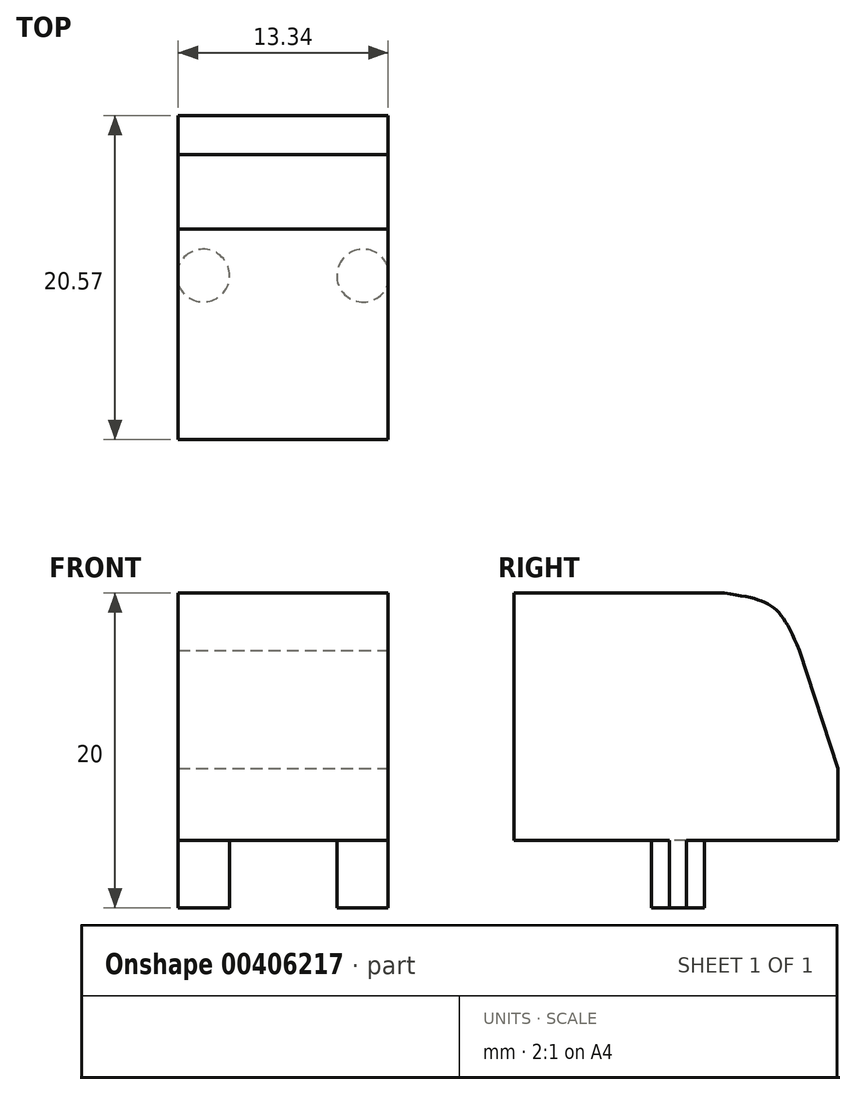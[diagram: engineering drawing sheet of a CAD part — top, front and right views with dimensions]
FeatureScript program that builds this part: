
annotation { "Feature Type Name" : "Feature", "Feature Type Description" : "" }
export const myFeature = defineFeature(function(context is Context, id is Id, definition is map)
    precondition{}
    {
        {
            var Q0;
            Q0=qCreatedBy(makeId("Front.planeOp"),FACE);
            var sketch = newSketch(context, id + "F0", { "sketchPlane" : qUnion([Q0])});
            skLineSegment(sketch, "E0.bottom", {"start": v(6.67, -7.85) * mm, "end": v(-6.67, -7.85) * mm});
            skLineSegment(sketch, "E0.top", {"start": v(6.67, 7.85) * mm, "end": v(-6.67, 7.85) * mm});
            skLineSegment(sketch, "E0.left", {"start": v(6.67, -7.85) * mm, "end": v(6.67, 7.85) * mm});
            skLineSegment(sketch, "E0.right", {"start": v(-6.67, -7.85) * mm, "end": v(-6.67, 7.85) * mm});
            skPoint(sketch, "E0.middle", {"position": v(0, 0) * mm});
            skSolve(sketch);
        }
        {
            var Q0;
            Q0=makeQuery(id+"F0.imprint","IMPRINT",FACE,{"disambiguationData":[TD([[makeQuery(id+"F0.imprint","IMPRINT",EDGE,{"derivedFrom":sQuery(id+"F0.wireOp",EDGE,"E0.bottom")}),-1.0]])]});
            extrude(context, id + "F1", {"entities" : qUnion([Q0]), "oppositeDirection" : true, "depth" : 20.57 * mm});
        }
        {
            var Q0;
            Q0=makeQuery(id+"F1.opExtrude","SWEPT_FACE",FACE,{"disambiguationData":[OSD([sQuery(id+"F0.wireOp",EDGE,"E0.bottom")])]});
            var sketch = newSketch(context, id + "F2", { "sketchPlane" : qUnion([Q0])});
            skLineSegment(sketch, "E1", {"start": v(0, 0) * mm, "end": v(0, -10.4) * mm, "construction": true});
            skPoint(sketch, "E1.endSnap0", {"position": v(0, 0) * mm});
            skLineSegment(sketch, "E2", {"start": v(0, -10.4) * mm, "end": v(5.08, -10.4) * mm, "construction": true});
            skLineSegment(sketch, "E3.MirrorCS", {"start": v(0, -10.4) * mm, "end": v(-5.08, -10.4) * mm, "construction": true});
            skCircle(sketch, "E4", {"center": v(5.08, -10.4) * mm, "radius": 1.68 * mm});
            skCircle(sketch, "E5", {"center": v(-5.08, -10.4) * mm, "radius": 1.68 * mm});
            skSolve(sketch);
        }
        {
            var Q0;
            {var subQ0=sQuery(id+"F2.wireOp",EDGE,"E4");var subQ1=makeQuery(id+"F1.opExtrude","SWEPT_EDGE",EDGE,{"disambiguationData":[OSD([sQuery(id+"F0.wireOp",EDGE,"E0.bottom"),sQuery(id+"F0.wireOp",EDGE,"E0.left")])]});var subQ2=makeQuery(id+"F2.imprint","INTERSECT",VERTEX,{"disambiguationData":[OD(0.0)],"derivedFrom":[subQ1,subQ0]});Q0=makeQuery(id+"F2.imprint","IMPRINT",FACE,{"disambiguationData":[TD([[makeQuery(id+"F2.imprint","IMPRINT",EDGE,{"disambiguationData":[TD([[subQ2,-1.0]])],"derivedFrom":subQ0}),1.0]])]});}
            var Q1;
            {var subQ0=sQuery(id+"F2.wireOp",EDGE,"E5");var subQ1=makeQuery(id+"F1.opExtrude","SWEPT_EDGE",EDGE,{"disambiguationData":[OSD([sQuery(id+"F0.wireOp",EDGE,"E0.bottom"),sQuery(id+"F0.wireOp",EDGE,"E0.right")])]});var subQ2=makeQuery(id+"F2.imprint","INTERSECT",VERTEX,{"disambiguationData":[OD(0.0)],"derivedFrom":[subQ1,subQ0]});Q1=makeQuery(id+"F2.imprint","IMPRINT",FACE,{"disambiguationData":[TD([[makeQuery(id+"F2.imprint","IMPRINT",EDGE,{"disambiguationData":[TD([[subQ2,1.0]])],"derivedFrom":subQ0}),1.0]])]});}
            extrude(context, id + "F3", {"entities" : qUnion([Q0, Q1]), "operationType" : NewBodyOperationType.ADD, "depth" : 4.3 * mm});
        }
        {
            var Q0;
            {var subQ0=sQuery(id+"F0.wireOp",EDGE,"E0.left");Q0=makeQuery(id+"F3.boolean.opBoolean","MERGE",FACE,{"derivedFrom":[makeQuery(id+"F1.opExtrude","SWEPT_FACE",FACE,{"disambiguationData":[OSD([subQ0])]}),makeQuery(id+"F3.opExtrude","SWEPT_FACE",FACE,{"disambiguationData":[OSD([sQuery(id+"F0.wireOp",EDGE,"E0.bottom"),subQ0])]})]});}
            var sketch = newSketch(context, id + "F4", { "sketchPlane" : qUnion([Q0])});
            skLineSegment(sketch, "E6", {"start": v(20.57, -3.28) * mm, "end": v(18.1, 4.2) * mm});
            skFitSpline(sketch, "E7", {"points": [v(18.1, 4.2) * mm, v(13.37, 7.85) * mm], "startDerivative": vector(-3.58, 9) * mm, "endDerivative": vector(-8.86, 1.39) * mm});
            skSolve(sketch);
        }
        {
            var Q0;
            {var subQ0=sQuery(id+"F4.wireOp",EDGE,"E6");Q0=makeQuery(id+"F4.imprint","IMPRINT",FACE,{"disambiguationData":[TD([[makeQuery(id+"F4.imprint","IMPRINT",EDGE,{"derivedFrom":subQ0}),-1.0]])]});}
            extrude(context, id + "F5", {"entities" : qUnion([Q0]), "operationType" : NewBodyOperationType.REMOVE, "endBound" : BoundingType.THROUGH_ALL, "oppositeDirection" : true, "depth" : 25.4 * mm});
        }
    });
